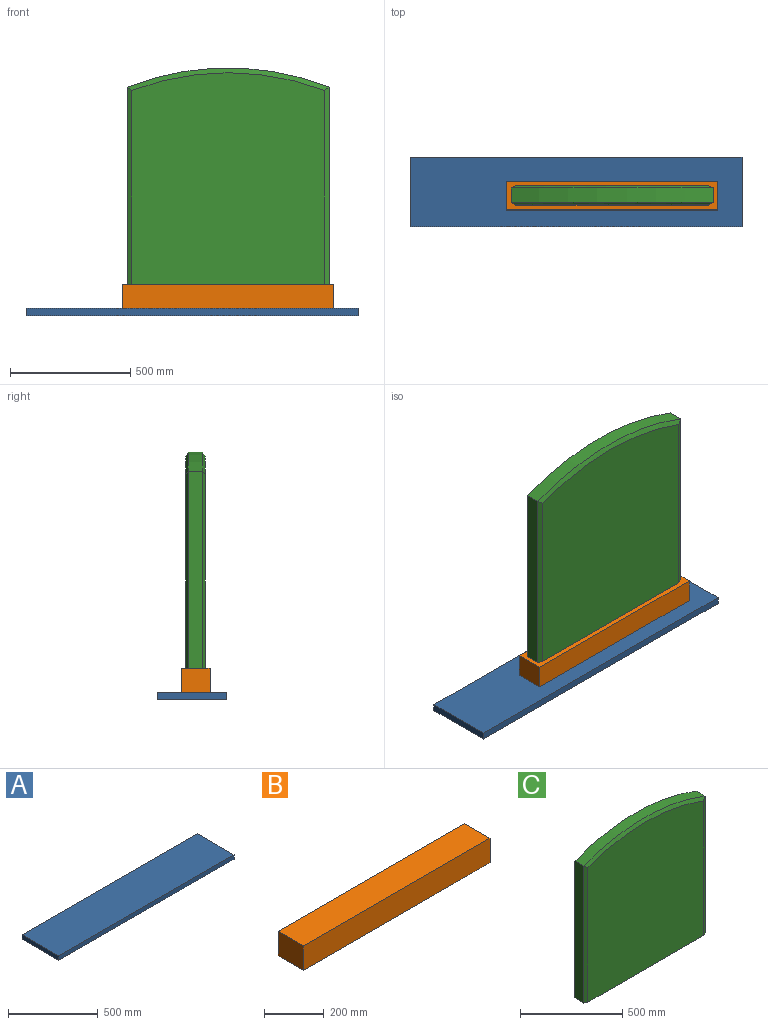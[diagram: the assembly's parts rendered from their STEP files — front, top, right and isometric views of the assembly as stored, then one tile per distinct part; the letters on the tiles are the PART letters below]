
ASSEMBLY  parts=3 mates=1
PART A: 6 faces, bbox 1380x290x30 mm
  f0: plane 290x30mm, normal (-1,0,0), area 8700mm2, adj f1,f3,f4,f5
  f1: plane 1380x30mm, normal (0,-1,0), area 41400mm2, adj f0,f2,f4,f5
  f2: plane 290x30mm, normal (1,0,0), area 8700mm2, adj f1,f3,f4,f5
  f3: plane 1380x30mm, normal (0,1,0), area 41400mm2, adj f0,f2,f4,f5
  f4: plane 1380x290mm, normal (0,0,1), area 400200mm2, adj f0,f1,f2,f3
  f5: plane 1380x290mm, normal (0,0,-1), area 400200mm2, adj f0,f1,f2,f3
PART B: 6 faces, bbox 880x120x100 mm
  f0: plane 880x120mm, normal (0,0,1), area 105600mm2, adj f1,f3,f4,f5
  f1: plane 120x100mm, normal (-1,0,0), area 12000mm2, adj f0,f2,f4,f5
  f2: plane 880x120mm, normal (0,0,-1), area 105600mm2, adj f1,f3,f4,f5
  f3: plane 120x100mm, normal (1,0,0), area 12000mm2, adj f0,f2,f4,f5
  f4: plane 880x100mm, normal (0,-1,0), area 88000mm2, adj f0,f1,f2,f3
  f5: plane 880x100mm, normal (0,1,0), area 88000mm2, adj f0,f1,f2,f3
PART C: 12 faces, bbox 840x80x900 mm
  f0: plane 819.81x60mm, normal (-1,0,0), area 49188.7mm2, adj f1,f3,f8,f9
  f1: plane 840x80mm, normal (0,0,-1), area 66800mm2, adj f0,f2,f4,f5,f6,f8,f9,f11
  f2: plane 819.81x60mm, normal (1,0,0), area 49188.7mm2, adj f1,f3,f6,f11
  f3: cylinder r=1140mm len=840mm, axis (0,1,0), area 51616mm2, adj f0,f2,f7,f10
  f4: plane 880x800mm, normal (0,-1,0), area 684570.2mm2, adj f1,f9,f10,f11
  f5: plane 880x800mm, normal (0,1,0), area 684570.2mm2, adj f1,f6,f7,f8
  f6: plane 819.81x20mm, normal (0.45,0.89,0), area 18179mm2, adj f1,f2,f5,f7
  f7: cone r=1140mm half-angle=63.4deg, axis (0,-1,0), area 18764.1mm2, adj f3,f5,f6,f8
  f8: plane 819.81x20mm, normal (-0.45,0.89,0), area 18179mm2, adj f0,f1,f5,f7
  f9: plane 819.81x20mm, normal (-0.45,-0.89,0), area 18179mm2, adj f0,f1,f4,f10
  f10: cone r=1120mm half-angle=63.4deg, axis (0,1,0), area 18764.1mm2, adj f3,f4,f9,f11
  f11: plane 819.81x20mm, normal (0.45,-0.89,0), area 18179mm2, adj f1,f2,f4,f10
PLACE A t=(-1380,0,0)mm
PLACE B t=(-540,1370,130)mm
PLACE C t=(-540,1370,130)mm
MATE fastened B.f0 <-> C.f1  axis (0,0,1) through (-540,1370,130)mm
